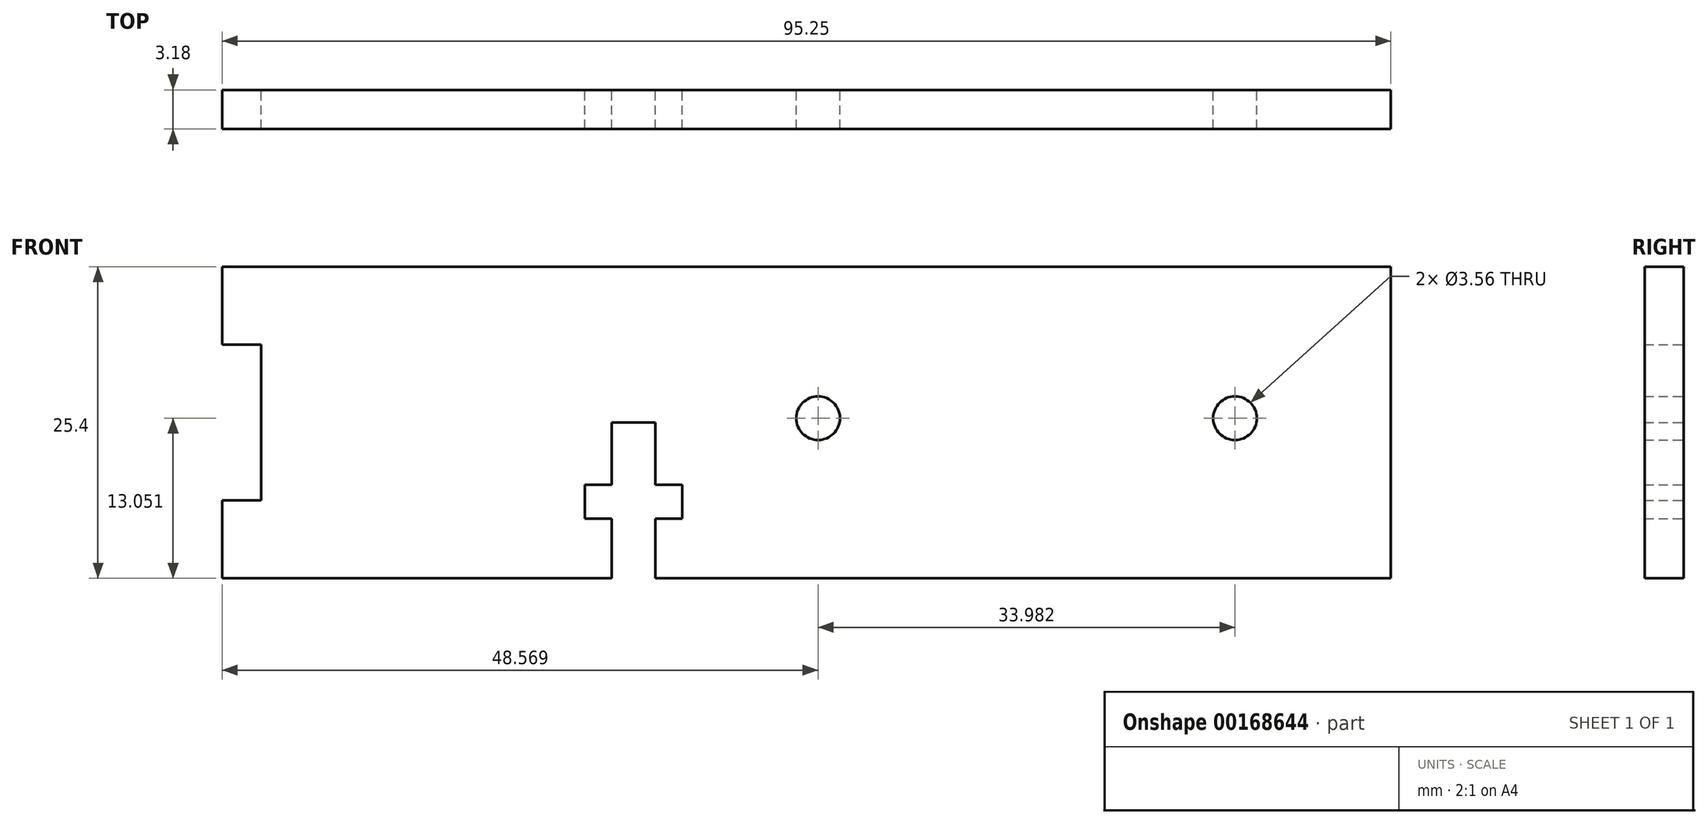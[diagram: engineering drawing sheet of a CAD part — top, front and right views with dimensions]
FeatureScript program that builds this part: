
annotation { "Feature Type Name" : "Feature", "Feature Type Description" : "" }
export const myFeature = defineFeature(function(context is Context, id is Id, definition is map)
    precondition{}
    {
        {
            var Q0;
            Q0=qCreatedBy(makeId("Front.planeOp"),FACE);
            var sketch = newSketch(context, id + "F0", { "sketchPlane" : qUnion([Q0])});
            skLineSegment(sketch, "E0.bottom", {"start": v(-44.9, -7.22) * mm, "end": v(50.35, -7.22) * mm});
            skLineSegment(sketch, "E0.top", {"start": v(-44.9, -32.62) * mm, "end": v(-13.15, -32.62) * mm});
            skLineSegment(sketch, "E0.left", {"start": v(-44.9, -7.22) * mm, "end": v(-44.9, -32.62) * mm});
            skLineSegment(sketch, "E0.right", {"start": v(50.35, -7.22) * mm, "end": v(50.35, -32.62) * mm});
            skCircle(sketch, "E1", {"center": v(37.65, -19.57) * mm, "radius": 1.78 * mm});
            skCircle(sketch, "E2", {"center": v(3.67, -19.57) * mm, "radius": 1.78 * mm});
            skLineSegment(sketch, "E3", {"start": v(-9.6, -32.62) * mm, "end": v(-9.6, -27.78) * mm});
            skLineSegment(sketch, "E4", {"start": v(-9.6, -27.78) * mm, "end": v(-7.4, -27.78) * mm});
            skLineSegment(sketch, "E5", {"start": v(-7.4, -27.78) * mm, "end": v(-7.4, -25) * mm});
            skLineSegment(sketch, "E6", {"start": v(-7.4, -25) * mm, "end": v(-9.6, -25) * mm});
            skLineSegment(sketch, "E7", {"start": v(-9.6, -25) * mm, "end": v(-9.6, -19.92) * mm});
            skLineSegment(sketch, "E8", {"start": v(-9.6, -19.92) * mm, "end": v(-13.15, -19.92) * mm});
            skLineSegment(sketch, "E9", {"start": v(-13.15, -25) * mm, "end": v(-15.34, -25) * mm});
            skLineSegment(sketch, "E10", {"start": v(-15.34, -25) * mm, "end": v(-15.34, -27.78) * mm});
            skLineSegment(sketch, "E11", {"start": v(-15.34, -27.78) * mm, "end": v(-13.15, -27.78) * mm});
            skLineSegment(sketch, "E12", {"start": v(-13.15, -27.78) * mm, "end": v(-13.15, -32.62) * mm});
            skLineSegment(sketch, "E13", {"start": v(-13.15, -19.92) * mm, "end": v(-13.15, -25) * mm});
            skLineSegment(sketch, "E14.bottom", {"start": v(-44.9, -13.57) * mm, "end": v(-41.72, -13.57) * mm});
            skLineSegment(sketch, "E14.top", {"start": v(-44.9, -26.27) * mm, "end": v(-41.72, -26.27) * mm});
            skLineSegment(sketch, "E14.left", {"start": v(-44.9, -13.57) * mm, "end": v(-44.9, -26.27) * mm});
            skLineSegment(sketch, "E14.right", {"start": v(-41.72, -13.57) * mm, "end": v(-41.72, -26.27) * mm});
            skLineSegment(sketch, "E15.trimOffspring", {"start": v(-9.6, -32.62) * mm, "end": v(50.35, -32.62) * mm});
            skSolve(sketch);
        }
        {
            var Q0;
            Q0=makeQuery(id+"F0.imprint","IMPRINT",FACE,{"disambiguationData":[TD([[makeQuery(id+"F0.imprint","IMPRINT",EDGE,{"derivedFrom":sQuery(id+"F0.wireOp",EDGE,"E0.bottom")}),-1.0]])]});
            extrude(context, id + "F1", {"entities" : qUnion([Q0]), "endBound" : BoundingType.SYMMETRIC, "depth" : 3.17 * mm});
        }
    });
